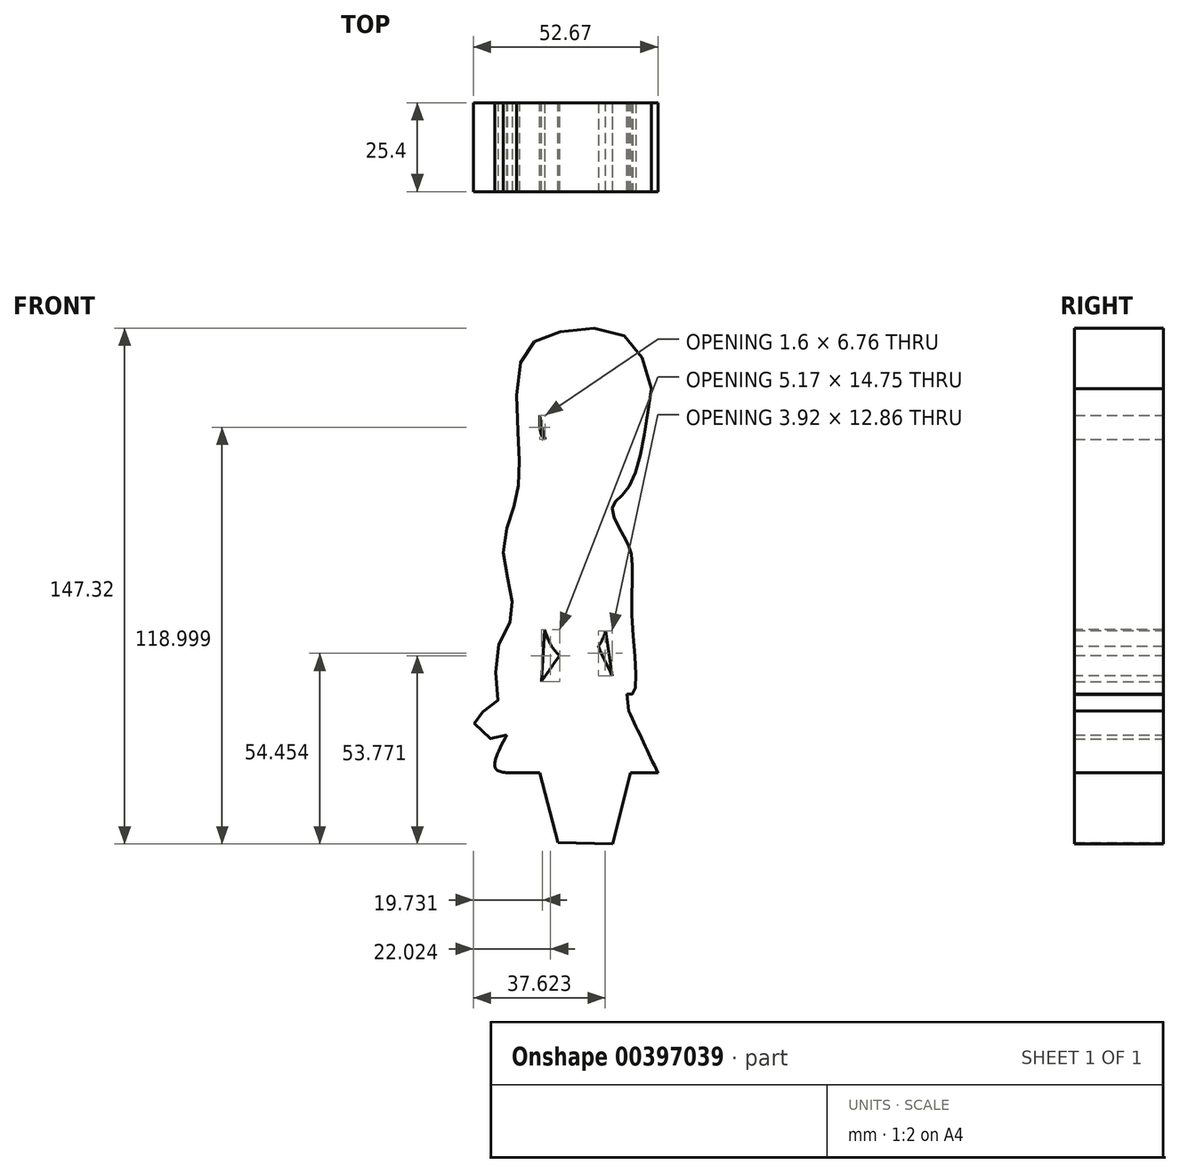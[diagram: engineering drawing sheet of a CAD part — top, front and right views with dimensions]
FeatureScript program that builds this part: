
annotation { "Feature Type Name" : "Feature", "Feature Type Description" : "" }
export const myFeature = defineFeature(function(context is Context, id is Id, definition is map)
    precondition{}
    {
        {
            var Q0;
            Q0=qCreatedBy(makeId("Front.planeOp"),FACE);
            var sketch = newSketch(context, id + "F0", { "sketchPlane" : qUnion([Q0])});
            skFitSpline(sketch, "E0", {"points": [v(-9.67, 65.8) * mm, v(9.86, 65.22) * mm, v(14.98, 56.31) * mm, v(12.32, 43.6) * mm, v(0, 30.71) * mm, v(-10.43, 38.49) * mm, v(-13.65, 55.55) * mm, v(-9.67, 65.8) * mm]});
            skFitSpline(sketch, "E1", {"points": [v(4.37, 32.83) * mm, v(3.03, 23.89) * mm, v(4.74, 16.3) * mm, v(7.4, 11.38) * mm], "startDerivative": vector(-5.7, -24.46) * mm, "endDerivative": vector(9.67, -15.85) * mm});
            skFitSpline(sketch, "E2", {"points": [v(-6.64, 33.36) * mm, v(-6.26, 25.4) * mm, v(-9.67, 16.87) * mm, v(-15.17, 12.9) * mm], "startDerivative": vector(3.34, -23.1) * mm, "endDerivative": vector(-19.23, -10.23) * mm});
            skFitSpline(sketch, "E3", {"points": [v(-15.17, 12.9) * mm, v(-3.41, 9.48) * mm, v(7.4, 11.38) * mm], "startDerivative": vector(23.05, -9.35) * mm, "endDerivative": vector(22.06, 6.46) * mm});
            skFitSpline(sketch, "E4", {"points": [v(7.4, 11.38) * mm, v(2.84, -18.77) * mm, v(-7.58, -20.48) * mm, v(-15.17, 12.9) * mm], "startDerivative": vector(0.92, -98.02) * mm, "endDerivative": vector(-7.52, 109.24) * mm});
            skFitSpline(sketch, "E5", {"points": [v(-7.58, -20.48) * mm, v(-25.97, -52.52) * mm, v(-22.37, -54.04) * mm], "startDerivative": vector(-39.1, -56.15) * mm, "endDerivative": vector(19.47, -1.73) * mm});
            skFitSpline(sketch, "E6", {"points": [v(-22.37, -54.04) * mm, v(20.48, -54.04) * mm], "startDerivative": vector(42.85, 0) * mm, "endDerivative": vector(42.85, 0) * mm});
            skFitSpline(sketch, "E7", {"points": [v(20.48, -54.04) * mm, v(3.47, -17.97) * mm], "startDerivative": vector(-16.95, 36.02) * mm, "endDerivative": vector(-16.95, 36.02) * mm});
            skFitSpline(sketch, "E8", {"points": [v(-15.17, 12.9) * mm, v(-17.42, -34.6) * mm], "startDerivative": vector(-2.25, -47.5) * mm, "endDerivative": vector(-2.25, -47.5) * mm});
            skFitSpline(sketch, "E9", {"points": [v(7.4, 11.38) * mm, v(12.15, -36.37) * mm], "startDerivative": vector(4.75, -47.75) * mm, "endDerivative": vector(4.75, -47.75) * mm});
            skFitSpline(sketch, "E10", {"points": [v(-11.8, -13.18) * mm, v(-12.75, -27.92) * mm], "startDerivative": vector(-0.93, -14.77) * mm, "endDerivative": vector(-0.93, -14.77) * mm});
            skFitSpline(sketch, "E11", {"points": [v(7.4, -26.3) * mm, v(5.6, -13.43) * mm], "startDerivative": vector(-1.8, 12.86) * mm, "endDerivative": vector(-1.8, 12.86) * mm});
            skFitSpline(sketch, "E12", {"points": [v(12.7, -54.04) * mm, v(7.58, -74.32) * mm], "startDerivative": vector(-5.12, -20.29) * mm, "endDerivative": vector(-5.12, -20.29) * mm});
            skFitSpline(sketch, "E13", {"points": [v(-13.27, -54.04) * mm, v(-8.09, -73.94) * mm], "startDerivative": vector(5.18, -19.9) * mm, "endDerivative": vector(5.18, -19.9) * mm});
            skFitSpline(sketch, "E14", {"points": [v(0, -54.04) * mm, v(0, -75.08) * mm], "startDerivative": vector(0, -21.05) * mm, "endDerivative": vector(0, -21.05) * mm});
            skFitSpline(sketch, "E15", {"points": [v(-8.09, -73.94) * mm, v(7.58, -74.32) * mm], "startDerivative": vector(15.67, -0.38) * mm, "endDerivative": vector(15.67, -0.38) * mm});
            skFitSpline(sketch, "E16", {"points": [v(18.58, 55.74) * mm, v(11.76, 26.92) * mm, v(7.58, 22.18) * mm, v(9.86, 15.17) * mm, v(12.9, 8.53) * mm, v(13.08, -9.67) * mm, v(13.65, -31.1) * mm, v(11.67, -31.54) * mm], "startDerivative": vector(-21.16, -156.02) * mm, "endDerivative": vector(-38.04, 5.87) * mm});
            skFitSpline(sketch, "E17", {"points": [v(18.58, 55.74) * mm, v(11.19, 70.72) * mm, v(-8.09, 71.86) * mm, v(-18.01, 65.22) * mm, v(-19.53, 43.99) * mm, v(-19.15, 29.39) * mm, v(-21.05, 20.67) * mm, v(-23.7, 10.24) * mm, v(-21.61, -1.9) * mm, v(-21.61, -10.62) * mm, v(-25.97, -21.61) * mm, v(-25.97, -35.08) * mm, v(-32.04, -37.92) * mm, v(-28.06, -43.99) * mm, v(-22.6, -43.17) * mm], "startDerivative": vector(-50.83, 212.21) * mm, "endDerivative": vector(106.3, 54.2) * mm});
            skFitSpline(sketch, "E18", {"points": [v(13.91, 60.8) * mm, v(-11.66, 41.3) * mm, v(-13.26, 48.06) * mm], "startDerivative": vector(-48.43, -45.55) * mm, "endDerivative": vector(-0.1, 29.17) * mm});
            skSolve(sketch);
        }
        {
            var Q0;
            {var subQ11=sQuery(id+"F0.wireOp",EDGE,"E1");Q0=makeQuery(id+"F0.imprint","IMPRINT",FACE,{"disambiguationData":[TD([[makeQuery(id+"F0.imprint","IMPRINT",EDGE,{"derivedFrom":subQ11}),1.0]])]});}
            var Q1;
            {var subQ0=sQuery(id+"F0.wireOp",EDGE,"E18");var subQ1=sQuery(id+"F0.wireOp",EDGE,"E0");var subQ2=makeQuery(id+"F0.imprint","INTERSECT",VERTEX,{"disambiguationData":[OD(1.0)],"derivedFrom":[subQ1,subQ0]});Q1=makeQuery(id+"F0.imprint","IMPRINT",FACE,{"disambiguationData":[TD([[makeQuery(id+"F0.imprint","IMPRINT",EDGE,{"disambiguationData":[TD([[subQ2,1.0]])],"derivedFrom":subQ1}),-1.0]])]});}
            var Q2;
            {var subQ0=sQuery(id+"F0.wireOp",EDGE,"E0");var subQ1=makeQuery(id+"F0.imprint","INTERSECT",VERTEX,{"derivedFrom":[subQ0,sQuery(id+"F0.wireOp",EDGE,"E1")]});Q2=makeQuery(id+"F0.imprint","IMPRINT",FACE,{"disambiguationData":[TD([[makeQuery(id+"F0.imprint","IMPRINT",EDGE,{"disambiguationData":[TD([[subQ1,1.0]])],"derivedFrom":subQ0}),-1.0]])]});}
            var Q3;
            {var subQ0=sQuery(id+"F0.wireOp",EDGE,"E1");Q3=makeQuery(id+"F0.imprint","IMPRINT",FACE,{"disambiguationData":[TD([[makeQuery(id+"F0.imprint","IMPRINT",EDGE,{"derivedFrom":subQ0}),-1.0]])]});}
            var Q4;
            {var subQ4=sQuery(id+"F0.wireOp",EDGE,"E3");Q4=makeQuery(id+"F0.imprint","IMPRINT",FACE,{"disambiguationData":[TD([[makeQuery(id+"F0.imprint","IMPRINT",EDGE,{"derivedFrom":subQ4}),-1.0]])]});}
            var Q5;
            {var subQ7=sQuery(id+"F0.wireOp",EDGE,"E5");var subQ10=sQuery(id+"F0.wireOp",EDGE,"E4");var subQ11=makeQuery(id+"F0.imprint","INTERSECT",VERTEX,{"derivedFrom":[subQ10,subQ7]});Q5=makeQuery(id+"F0.imprint","IMPRINT",FACE,{"disambiguationData":[TD([[makeQuery(id+"F0.imprint","IMPRINT",EDGE,{"disambiguationData":[TD([[subQ11,1.0]])],"derivedFrom":subQ10}),1.0]])]});}
            var Q6;
            {var subQ0=sQuery(id+"F0.wireOp",EDGE,"E12");Q6=makeQuery(id+"F0.imprint","IMPRINT",FACE,{"disambiguationData":[TD([[makeQuery(id+"F0.imprint","IMPRINT",EDGE,{"derivedFrom":subQ0}),-1.0]])]});}
            var Q7;
            {var subQ0=sQuery(id+"F0.wireOp",EDGE,"E13");Q7=makeQuery(id+"F0.imprint","IMPRINT",FACE,{"disambiguationData":[TD([[makeQuery(id+"F0.imprint","IMPRINT",EDGE,{"derivedFrom":subQ0}),1.0]])]});}
            var Q8;
            {var subQ4=sQuery(id+"F0.wireOp",EDGE,"E11");Q8=makeQuery(id+"F0.imprint","IMPRINT",FACE,{"disambiguationData":[TD([[makeQuery(id+"F0.imprint","IMPRINT",EDGE,{"derivedFrom":subQ4}),-1.0]])]});}
            extrude(context, id + "F1", {"entities" : qUnion([Q0, Q1, Q2, Q3, Q4, Q5, Q6, Q7, Q8]), "depth" : 25.4 * mm});
        }
    });
